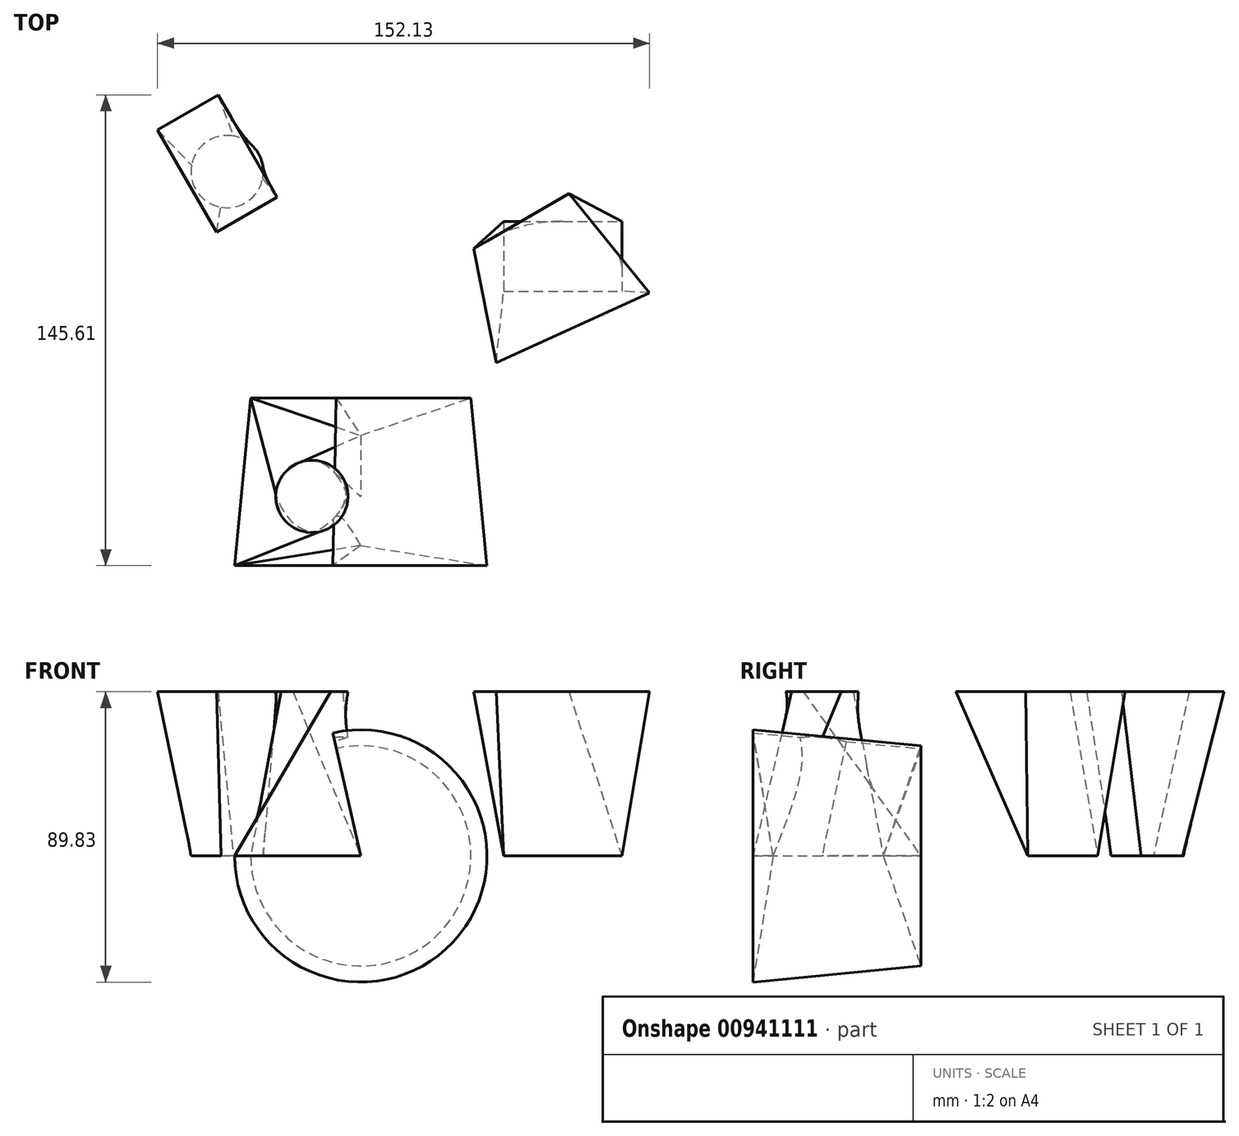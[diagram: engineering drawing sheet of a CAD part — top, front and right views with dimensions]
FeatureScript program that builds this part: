
annotation { "Feature Type Name" : "Feature", "Feature Type Description" : "" }
export const myFeature = defineFeature(function(context is Context, id is Id, definition is map)
    precondition{}
    {
        {
            var Q0;
            Q0=qCreatedBy(makeId("Top.planeOp"),FACE);
            var sketch = newSketch(context, id + "F0", { "sketchPlane" : qUnion([Q0])});
            skCircle(sketch, "E0", {"center": v(-62.28, 52.52) * mm, "radius": 11.18 * mm});
            skLineSegment(sketch, "E1.bottom", {"start": v(23.25, 37.16) * mm, "end": v(59.79, 37.16) * mm});
            skLineSegment(sketch, "E1.top", {"start": v(23.25, 15.57) * mm, "end": v(59.79, 15.57) * mm});
            skLineSegment(sketch, "E1.left", {"start": v(23.25, 37.16) * mm, "end": v(23.25, 15.57) * mm});
            skLineSegment(sketch, "E1.right", {"start": v(59.79, 37.16) * mm, "end": v(59.79, 15.57) * mm});
            skLineSegment(sketch, "E2", {"start": v(-55, -17.45) * mm, "end": v(-20.95, -29.08) * mm});
            skLineSegment(sketch, "E3", {"start": v(-20.95, -29.08) * mm, "end": v(-20.95, -63.13) * mm});
            skLineSegment(sketch, "E4", {"start": v(-20.95, -63.13) * mm, "end": v(-59.98, -69.35) * mm});
            skLineSegment(sketch, "E5", {"start": v(-59.98, -69.35) * mm, "end": v(-55, -17.45) * mm});
            skLineSegment(sketch, "E6", {"start": v(-82.91, 71.7) * mm, "end": v(-82.91, 30.26) * mm, "construction": true});
            skSolve(sketch);
        }
        {
            var Q0;
            Q0=qCreatedBy(makeId("Top.planeOp"),FACE);
            cPlane(context, id + "F1", {"entities" : qUnion([Q0]), "cplaneType" : CPlaneType.OFFSET, "offset" : 50.8 * mm, "width" : 152.4 * mm, "height" : 152.4 * mm});
        }
        {
            var Q0;
            Q0=qCreatedBy(id+"F1.planeOp",FACE);
            var sketch = newSketch(context, id + "F2", { "sketchPlane" : qUnion([Q0])});
            skCircle(sketch, "E7.0", {"center": v(-36.07, -47.94) * mm, "radius": 11.18 * mm});
            skLineSegment(sketch, "E7.1.0", {"start": v(-65.53, 33.82) * mm, "end": v(-46.83, 44.61) * mm});
            skLineSegment(sketch, "E7.1.1", {"start": v(-46.83, 44.61) * mm, "end": v(-65.1, 76.26) * mm});
            skLineSegment(sketch, "E7.1.2", {"start": v(-65.1, 76.26) * mm, "end": v(-83.8, 65.46) * mm});
            skLineSegment(sketch, "E7.1.3", {"start": v(-83.8, 65.46) * mm, "end": v(-65.53, 33.82) * mm});
            skLineSegment(sketch, "E7.2.0", {"start": v(20.9, -6.64) * mm, "end": v(68.33, 15) * mm});
            skLineSegment(sketch, "E7.2.1", {"start": v(68.33, 15) * mm, "end": v(43.42, 45.68) * mm});
            skLineSegment(sketch, "E7.2.2", {"start": v(43.42, 45.68) * mm, "end": v(13.94, 28.66) * mm});
            skLineSegment(sketch, "E7.2.3", {"start": v(13.94, 28.66) * mm, "end": v(20.9, -6.64) * mm});
            skSolve(sketch);
        }
        {
            var Q0;
            Q0=makeQuery(id+"F2.imprint","IMPRINT",FACE,{"disambiguationData":[TD([[makeQuery(id+"F2.imprint","IMPRINT",EDGE,{"derivedFrom":sQuery(id+"F2.wireOp",EDGE,"E7.2.0")}),1.0]])]});
            var Q1;
            Q1=makeQuery(id+"F0.imprint","IMPRINT",FACE,{"disambiguationData":[TD([[makeQuery(id+"F0.imprint","IMPRINT",EDGE,{"derivedFrom":sQuery(id+"F0.wireOp",EDGE,"E1.bottom")}),-1.0]])]});
            loft(context, id + "F3", {"sheetProfilesArray" : [{ "sheetProfileEntities" : qUnion([Q0]) }, { "sheetProfileEntities" : qUnion([Q1]) }]});
        }
        {
            var Q0;
            Q0=makeQuery(id+"F2.imprint","IMPRINT",FACE,{"disambiguationData":[TD([[makeQuery(id+"F2.imprint","IMPRINT",EDGE,{"derivedFrom":sQuery(id+"F2.wireOp",EDGE,"E7.0")}),1.0]])]});
            var Q1;
            Q1=makeQuery(id+"F0.imprint","IMPRINT",FACE,{"disambiguationData":[TD([[makeQuery(id+"F0.imprint","IMPRINT",EDGE,{"derivedFrom":sQuery(id+"F0.wireOp",EDGE,"E2")}),-1.0]])]});
            loft(context, id + "F4", {"sheetProfilesArray" : [{ "sheetProfileEntities" : qUnion([Q0]) }, { "sheetProfileEntities" : qUnion([Q1]) }]});
        }
        {
            var Q0;
            Q0=makeQuery(id+"F2.imprint","IMPRINT",FACE,{"disambiguationData":[TD([[makeQuery(id+"F2.imprint","IMPRINT",EDGE,{"derivedFrom":sQuery(id+"F2.wireOp",EDGE,"E7.1.0")}),1.0]])]});
            var Q1;
            Q1=makeQuery(id+"F0.imprint","IMPRINT",FACE,{"disambiguationData":[TD([[makeQuery(id+"F0.imprint","IMPRINT",EDGE,{"derivedFrom":sQuery(id+"F0.wireOp",EDGE,"E0")}),1.0]])]});
            loft(context, id + "F5", {"sheetProfilesArray" : [{ "sheetProfileEntities" : qUnion([Q0]) }, { "sheetProfileEntities" : qUnion([Q1]) }]});
        }
        {
            var Q0;
            Q0=makeQuery(id+"F0.imprint","IMPRINT",FACE,{"disambiguationData":[TD([[makeQuery(id+"F0.imprint","IMPRINT",EDGE,{"derivedFrom":sQuery(id+"F0.wireOp",EDGE,"E2")}),-1.0]])]});
            var Q1;
            Q1=sQuery(id+"F0.wireOp",EDGE,"E3");
            revolve(context, id + "F6", {"operationType" : NewBodyOperationType.ADD, "surfaceOperationType" : NewSurfaceOperationType.NEW, "entities" : qUnion([Q0]), "axis" : qUnion([Q1]), "revolveType" : RevolveType.ONE_DIRECTION, "angle" : 282.88 * degree});
        }
    });
